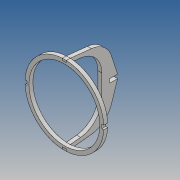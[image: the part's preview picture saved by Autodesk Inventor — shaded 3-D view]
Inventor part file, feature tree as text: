
AUTODESK INVENTOR PART (.ipt)
format: ipt  version: 2017 (Build 210142000, 142)  size: 159,232 bytes
history: native  units: mm
features: other x2, extrude x2, sketch x2
ambient origin geometry x8: Origin, YZ Plane, XZ Plane, XY Plane, X Axis, Y Axis, Z Axis, Center Point
bodies: Body1 (feature_tree), Body2 (feature_tree)
feature tree (6):
  other  "Sólido1"
  extrude  "Extrusión1"  Depth=5.0mm
  extrude  "Extrusión2"  Depth=5.0mm
  sketch  "Boceto1"  dims[d0=5.0mm d2=2.5mm]
  sketch  "Boceto2"  dims[d4=40.0mm d6=360.0deg d8=5.0mm d9=5.0mm d10=0.0mm d11=2.094395mm d12=40.0mm d13=90.0mm d14=5.0mm d15=20.0mm d16=10.0mm d17=3.141593mm d18=30.0mm d19=5.0mm d20=0.0mm]
  other  "Sólido2"
